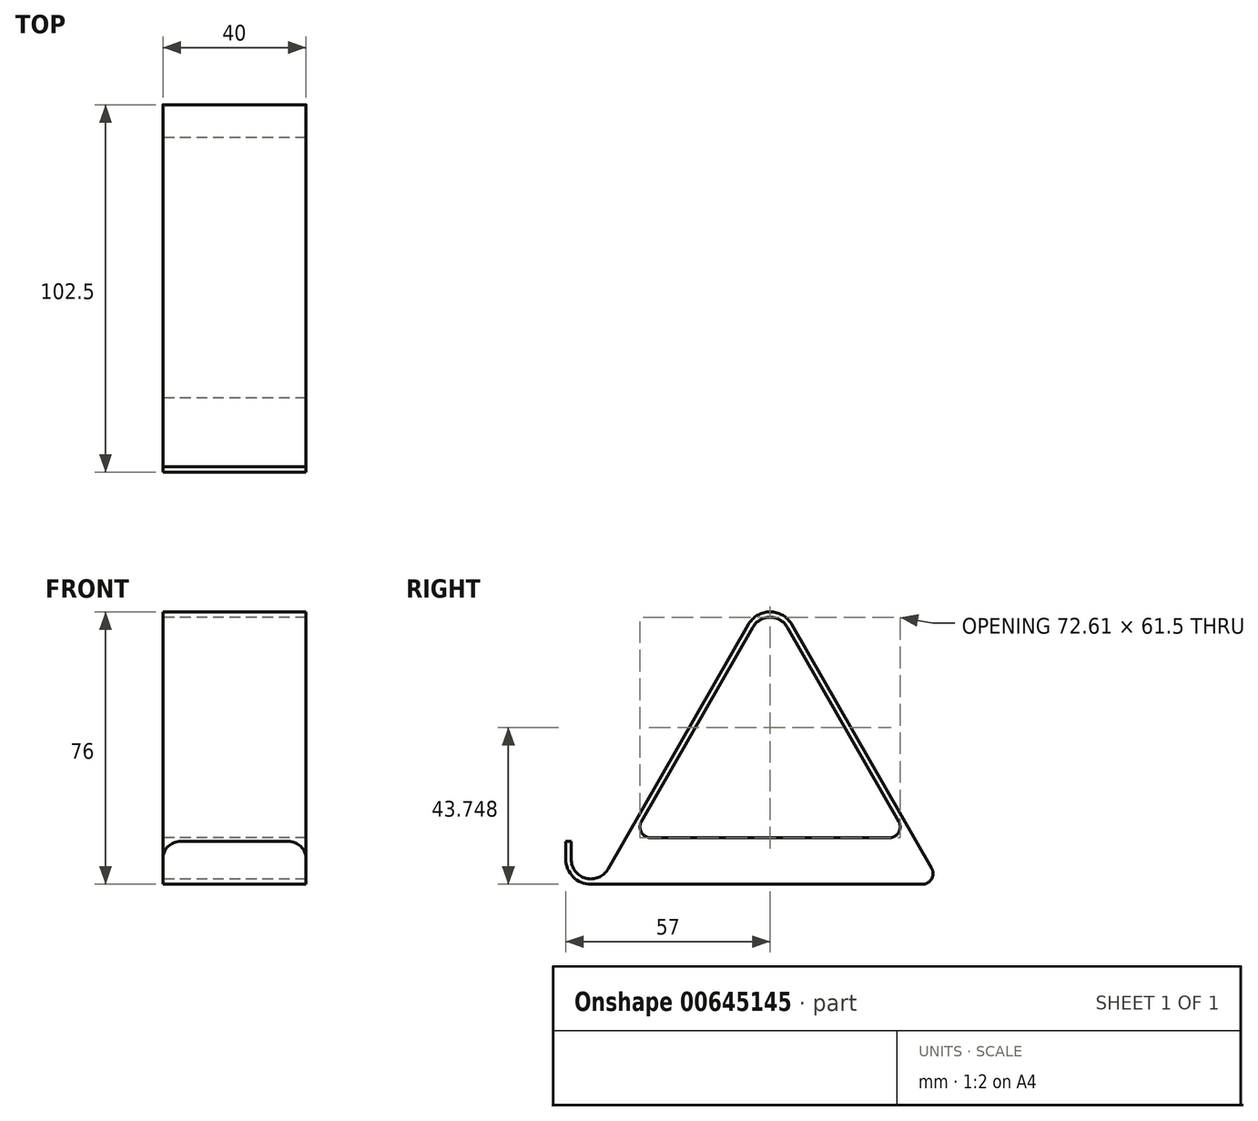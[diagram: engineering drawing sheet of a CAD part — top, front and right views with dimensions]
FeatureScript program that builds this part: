
annotation { "Feature Type Name" : "Feature", "Feature Type Description" : "" }
export const myFeature = defineFeature(function(context is Context, id is Id, definition is map)
    precondition{}
    {
        {
            var Q0;
            Q0=qCreatedBy(makeId("Right.planeOp"),FACE);
            var sketch = newSketch(context, id + "F0", { "sketchPlane" : qUnion([Q0])});
            skArc(sketch, "E0", {"start": v(-7, 0) * mm, "mid": v(-4.95, -4.95) * mm, "end": v(0, -7) * mm});
            skArc(sketch, "E1", {"start": v(54.77, 64.74) * mm, "mid": v(50, 67.5) * mm, "end": v(45.23, 64.74) * mm});
            skLineSegment(sketch, "E2", {"start": v(14.1, 10.49) * mm, "end": v(45.23, 64.74) * mm});
            skLineSegment(sketch, "E3", {"start": v(50, 62) * mm, "end": v(50, -46.3) * mm, "construction": true});
            skLineSegment(sketch, "E4.MirrorCS", {"start": v(85.9, 10.49) * mm, "end": v(54.77, 64.74) * mm});
            skLineSegment(sketch, "E5", {"start": v(-7, 0) * mm, "end": v(-7, 5) * mm});
            skLineSegment(sketch, "E6.0", {"start": v(-5.5, 0) * mm, "end": v(-5.5, 5) * mm});
            skLineSegment(sketch, "E6.1", {"start": v(95.1, -2.5) * mm, "end": v(56.07, 65.48) * mm});
            skArc(sketch, "E6.2", {"start": v(56.07, 65.48) * mm, "mid": v(50, 69) * mm, "end": v(43.93, 65.48) * mm});
            skLineSegment(sketch, "E6.3", {"start": v(4.77, -2.74) * mm, "end": v(43.93, 65.48) * mm});
            skArc(sketch, "E6.4", {"start": v(-5.5, 0) * mm, "mid": v(-1.42, -5.31) * mm, "end": v(4.77, -2.74) * mm});
            skLineSegment(sketch, "E7", {"start": v(-7, 5) * mm, "end": v(-5.5, 5) * mm});
            skLineSegment(sketch, "E8", {"start": v(0, -7) * mm, "end": v(92.5, -7) * mm});
            skLineSegment(sketch, "E9.0", {"start": v(16.7, 6) * mm, "end": v(83.3, 6) * mm});
            skPoint(sketch, "E10.visualSharp", {"position": v(11.51, 6) * mm});
            skArc(sketch, "E10.filletArc", {"start": v(14.1, 10.49) * mm, "mid": v(14.1, 7.5) * mm, "end": v(16.7, 6) * mm});
            skPoint(sketch, "E11.visualSharp", {"position": v(88.49, 6) * mm});
            skArc(sketch, "E11.filletArc", {"start": v(83.3, 6) * mm, "mid": v(85.9, 7.5) * mm, "end": v(85.9, 10.49) * mm});
            skPoint(sketch, "E12.visualSharp", {"position": v(97.68, -7) * mm});
            skArc(sketch, "E12.filletArc", {"start": v(92.5, -7) * mm, "mid": v(95.1, -5.5) * mm, "end": v(95.1, -2.5) * mm});
            skSolve(sketch);
        }
        {
            var Q0;
            Q0=makeQuery(id+"F0.imprint","IMPRINT",FACE,{"disambiguationData":[TD([[makeQuery(id+"F0.imprint","IMPRINT",EDGE,{"derivedFrom":sQuery(id+"F0.wireOp",EDGE,"E0")}),1.0]])]});
            extrude(context, id + "F1", {"entities" : qUnion([Q0]), "depth" : 40 * mm, "offsetDistance" : 25 * mm});
        }
        {
            var Q0;
            Q0=makeQuery(id+"F1.opExtrude","CAP_EDGE",EDGE,{"disambiguationData":[OSD([sQuery(id+"F0.wireOp",EDGE,"E7")])],"isStart":false});
            var Q1;
            Q1=makeQuery(id+"F1.opExtrude","CAP_EDGE",EDGE,{"disambiguationData":[OSD([sQuery(id+"F0.wireOp",EDGE,"E7")])],"isStart":true});
            fillet(context, id + "F2", {"entities" : qUnion([Q0, Q1]), "radius" : 5 * mm, "tangentPropagation" : true, "allowEdgeOverflow" : false});
        }
    });
